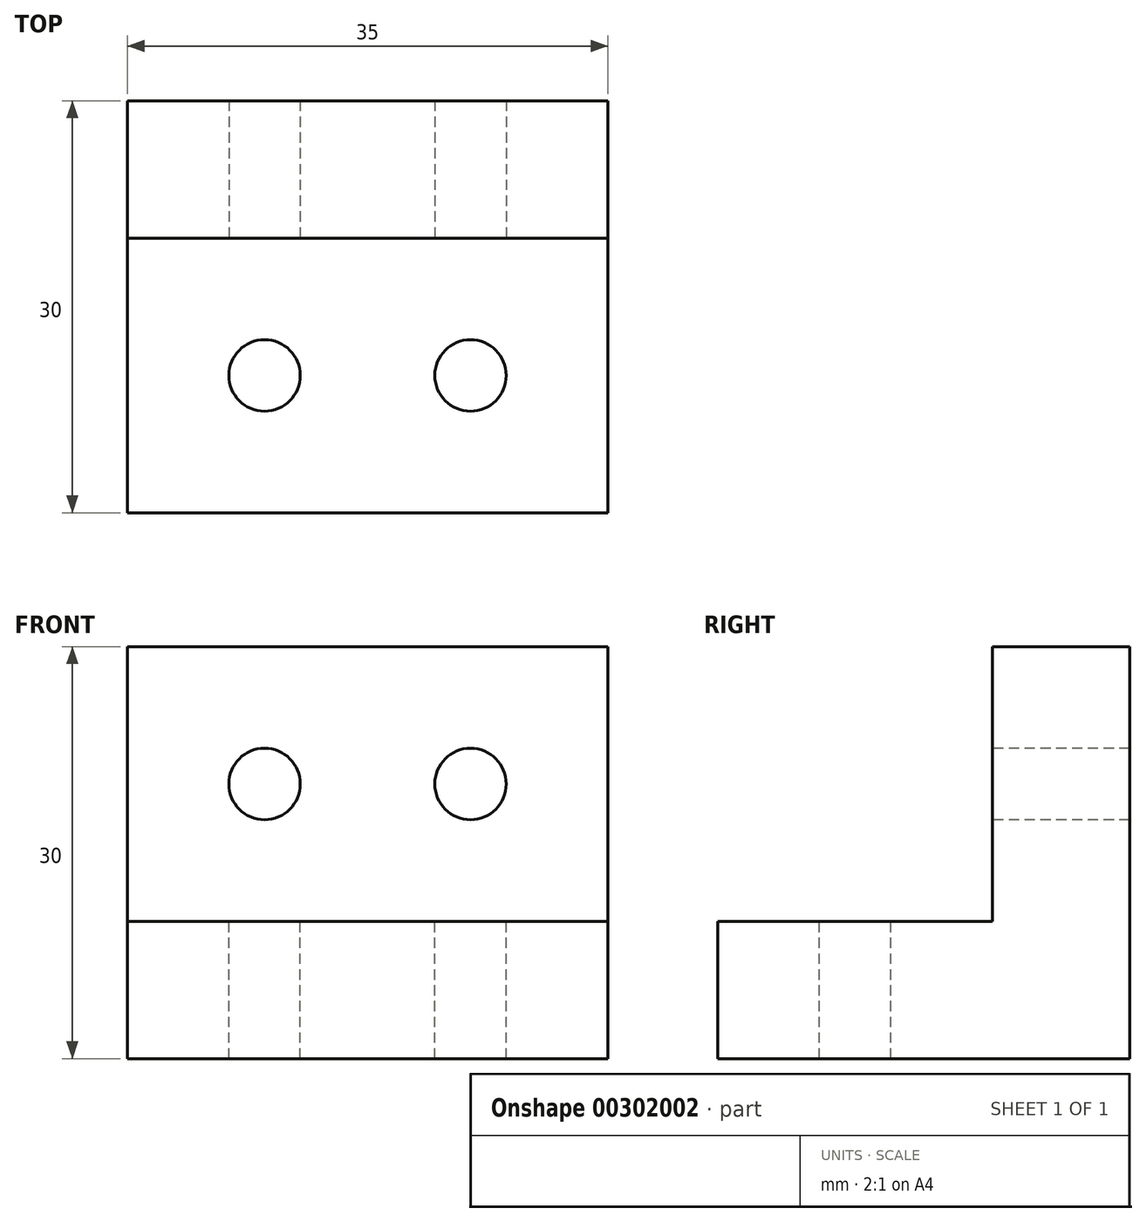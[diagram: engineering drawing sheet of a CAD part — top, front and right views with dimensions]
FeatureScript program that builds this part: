
annotation { "Feature Type Name" : "Feature", "Feature Type Description" : "" }
export const myFeature = defineFeature(function(context is Context, id is Id, definition is map)
    precondition{}
    {
        {
            var Q0;
            Q0=qCreatedBy(makeId("Right.planeOp"),FACE);
            var sketch = newSketch(context, id + "F0", { "sketchPlane" : qUnion([Q0])});
            skLineSegment(sketch, "E0", {"start": v(0, 0) * mm, "end": v(-30, 0) * mm});
            skLineSegment(sketch, "E1", {"start": v(-30, 0) * mm, "end": v(-30, 10) * mm});
            skLineSegment(sketch, "E2", {"start": v(-30, 10) * mm, "end": v(-10, 10) * mm});
            skLineSegment(sketch, "E3", {"start": v(-10, 10) * mm, "end": v(-10, 30) * mm});
            skLineSegment(sketch, "E4", {"start": v(-10, 30) * mm, "end": v(0, 30) * mm});
            skLineSegment(sketch, "E5", {"start": v(0, 30) * mm, "end": v(0, 0) * mm});
            skSolve(sketch);
        }
        {
            var Q0;
            Q0 = qSketchRegion(id + "F0", true);
            extrude(context, id + "F1", {"entities" : qUnion([Q0]), "depth" : (35 / 2) * mm, "hasSecondDirection" : true, "secondDirectionOppositeDirection" : true, "secondDirectionDepth" : (35 / 2) * mm});
        }
        {
            var Q0;
            Q0=makeQuery(id+"F1.opExtrude","SWEPT_FACE",FACE,{"disambiguationData":[OSD([sQuery(id+"F0.wireOp",EDGE,"E3")])]});
            var sketch = newSketch(context, id + "F2", { "sketchPlane" : qUnion([Q0])});
            skCircle(sketch, "E6", {"center": v(-7.5, 20) * mm, "radius": 2.6 * mm});
            skCircle(sketch, "E7", {"center": v(7.5, 20) * mm, "radius": 2.6 * mm});
            skSolve(sketch);
        }
        {
            var Q0;
            Q0 = qSketchRegion(id + "F2", true);
            extrude(context, id + "F3", {"entities" : qUnion([Q0]), "operationType" : NewBodyOperationType.REMOVE, "endBound" : BoundingType.THROUGH_ALL, "oppositeDirection" : true, "depth" : 25 * mm});
        }
        {
            var Q0;
            Q0=makeQuery(id+"F1.opExtrude","SWEPT_FACE",FACE,{"disambiguationData":[OSD([sQuery(id+"F0.wireOp",EDGE,"E2")])]});
            var sketch = newSketch(context, id + "F4", { "sketchPlane" : qUnion([Q0])});
            skCircle(sketch, "E8", {"center": v(-7.5, -20) * mm, "radius": 2.6 * mm});
            skCircle(sketch, "E9", {"center": v(7.5, -20) * mm, "radius": 2.6 * mm});
            skSolve(sketch);
        }
        {
            var Q0;
            Q0 = qSketchRegion(id + "F4", true);
            extrude(context, id + "F5", {"entities" : qUnion([Q0]), "operationType" : NewBodyOperationType.REMOVE, "endBound" : BoundingType.THROUGH_ALL, "oppositeDirection" : true, "depth" : 25 * mm});
        }
    });
